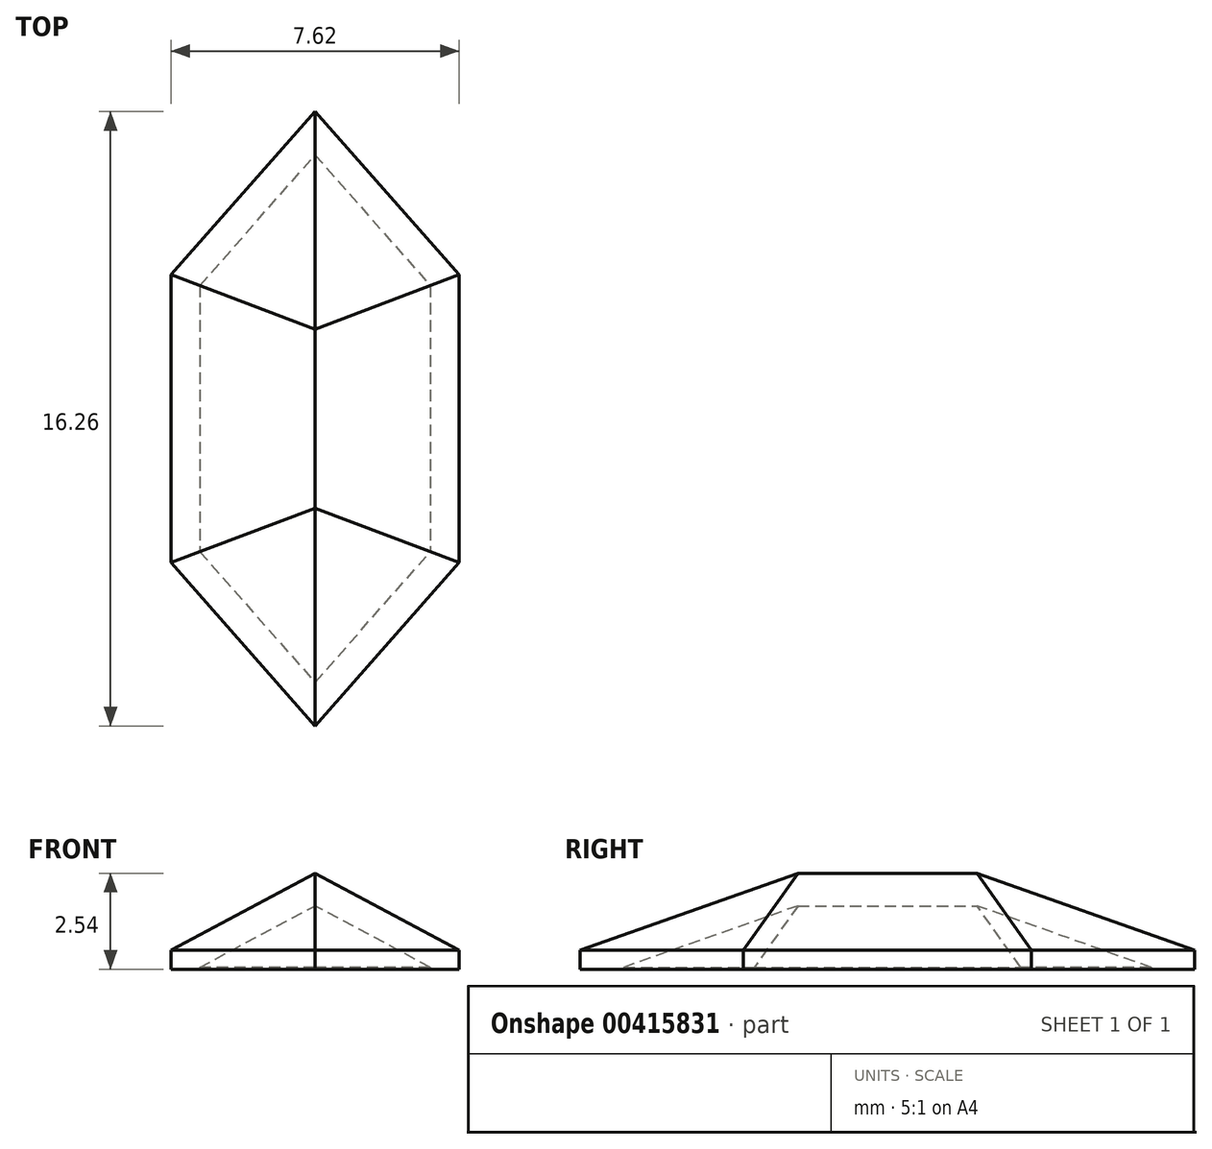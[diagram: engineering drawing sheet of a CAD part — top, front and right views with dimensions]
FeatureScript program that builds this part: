
annotation { "Feature Type Name" : "Feature", "Feature Type Description" : "" }
export const myFeature = defineFeature(function(context is Context, id is Id, definition is map)
    precondition{}
    {
        {
            var Q0;
            Q0=qCreatedBy(makeId("Top.planeOp"),FACE);
            var sketch = newSketch(context, id + "F0", { "sketchPlane" : qUnion([Q0])});
            skLineSegment(sketch, "E0.bottom", {"start": v(3.81, 3.81) * mm, "end": v(-3.81, 3.81) * mm});
            skLineSegment(sketch, "E0.top", {"start": v(3.81, -3.81) * mm, "end": v(-3.81, -3.81) * mm});
            skLineSegment(sketch, "E0.left", {"start": v(3.81, 3.81) * mm, "end": v(3.81, -3.81) * mm});
            skLineSegment(sketch, "E0.right", {"start": v(-3.81, 3.81) * mm, "end": v(-3.81, -3.81) * mm});
            skPoint(sketch, "E0.middle", {"position": v(0, 0) * mm});
            skLineSegment(sketch, "E1", {"start": v(-3.81, 3.8) * mm, "end": v(0, 8.13) * mm});
            skPoint(sketch, "E1.endSnap0", {"position": v(0, 3.81) * mm});
            skLineSegment(sketch, "E2", {"start": v(0, 8.13) * mm, "end": v(3.81, 3.8) * mm});
            skLineSegment(sketch, "E3.MirrorCS", {"start": v(0, -8.13) * mm, "end": v(3.81, -3.8) * mm});
            skLineSegment(sketch, "E4.MirrorCS", {"start": v(-3.81, -3.8) * mm, "end": v(0, -8.13) * mm});
            skSolve(sketch);
        }
        {
            var Q0;
            Q0=qSketchRegion(id+"F0",true);
            extrude(context, id + "F1", {"entities" : qUnion([Q0]), "depth" : 2.54 * mm});
        }
        {
            var Q0;
            Q0=makeQuery(id+"F1.opExtrude","CAP_EDGE",EDGE,{"disambiguationData":[OSD([sQuery(id+"F0.wireOp",EDGE,"E0.left")])],"isStart":false});
            var Q1;
            Q1=makeQuery(id+"F1.opExtrude","CAP_EDGE",EDGE,{"disambiguationData":[OSD([sQuery(id+"F0.wireOp",EDGE,"E2")])],"isStart":false});
            var Q2;
            Q2=makeQuery(id+"F1.opExtrude","CAP_EDGE",EDGE,{"disambiguationData":[OSD([sQuery(id+"F0.wireOp",EDGE,"E4.MirrorCS")])],"isStart":false});
            var Q3;
            Q3=makeQuery(id+"F1.opExtrude","CAP_EDGE",EDGE,{"disambiguationData":[OSD([sQuery(id+"F0.wireOp",EDGE,"E0.right")])],"isStart":false});
            var Q4;
            Q4=makeQuery(id+"F1.opExtrude","CAP_EDGE",EDGE,{"disambiguationData":[OSD([sQuery(id+"F0.wireOp",EDGE,"E1")])],"isStart":false});
            var Q5;
            Q5=makeQuery(id+"F1.opExtrude","CAP_EDGE",EDGE,{"disambiguationData":[OSD([sQuery(id+"F0.wireOp",EDGE,"E3.MirrorCS")])],"isStart":false});
            chamfer(context, id + "F2", {"entities" : qUnion([Q0, Q1, Q2, Q3, Q4, Q5]), "chamferType" : ChamferType.TWO_OFFSETS, "width1" : 2.03 * mm, "oppositeDirection" : false, "width2" : 3.8 * mm, "tangentPropagation" : true});
        }
        {
            var Q0;
            Q0=makeQuery(id+"F1.opExtrude","CAP_FACE",FACE,{"disambiguationData":[OSD([sQuery(id+"F0.wireOp",EDGE,"E0.left"),sQuery(id+"F0.wireOp",EDGE,"E0.right"),sQuery(id+"F0.wireOp",EDGE,"E1"),sQuery(id+"F0.wireOp",EDGE,"E2"),sQuery(id+"F0.wireOp",EDGE,"E3.MirrorCS"),sQuery(id+"F0.wireOp",EDGE,"E4.MirrorCS")])],"isStart":true});
            shell(context, id + "F3", {"entities" : qUnion([Q0]), "thickness" : 0.76 * mm});
        }
    });
